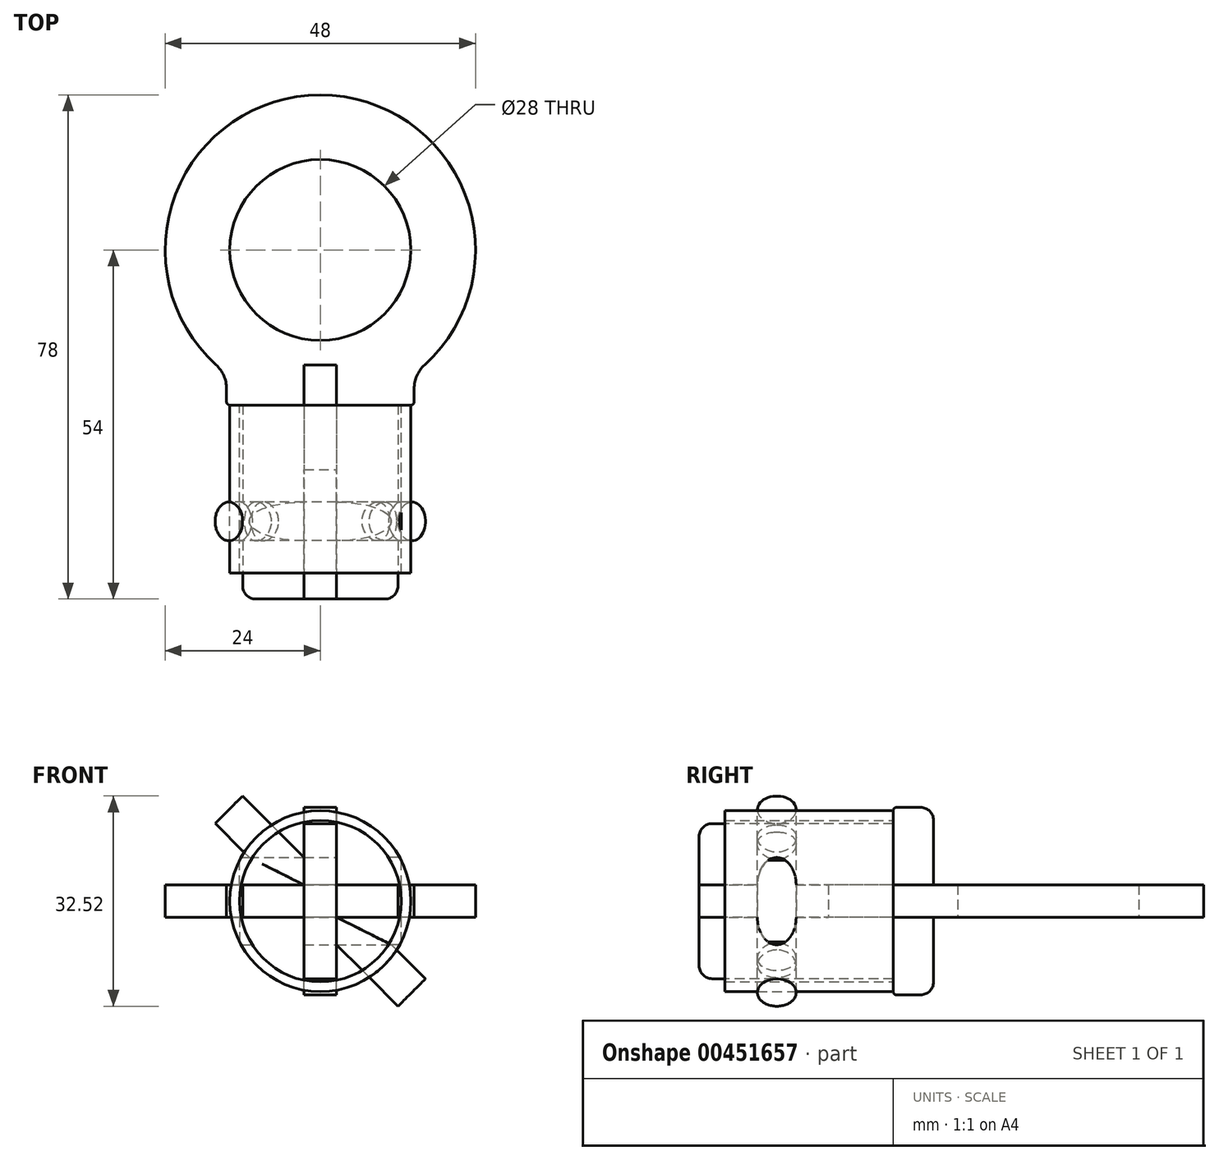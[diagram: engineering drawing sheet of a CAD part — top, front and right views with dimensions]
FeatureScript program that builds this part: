
annotation { "Feature Type Name" : "Feature", "Feature Type Description" : "" }
export const myFeature = defineFeature(function(context is Context, id is Id, definition is map)
    precondition{}
    {
        {
            var Q0;
            Q0=qCreatedBy(makeId("Top.planeOp"),FACE);
            var sketch = newSketch(context, id + "F0", { "sketchPlane" : qUnion([Q0])});
            skArc(sketch, "E0", {"start": v(15.27, -18.51) * mm, "mid": v(0.57, 24) * mm, "end": v(-16.14, -17.76) * mm});
            skLineSegment(sketch, "E1.top", {"start": v(-12, -54) * mm, "end": v(-2.5, -54) * mm});
            skLineSegment(sketch, "E1.left", {"start": v(-12, -24) * mm, "end": v(-12, -54) * mm});
            skCircle(sketch, "E2.converted", {"center": v(0, 0) * mm, "radius": 14 * mm});
            skLineSegment(sketch, "E3.top", {"start": v(-14.5, -24) * mm, "end": v(-12, -24) * mm});
            skLineSegment(sketch, "E3.left", {"start": v(-14.5, -21.47) * mm, "end": v(-14.5, -24) * mm});
            skPoint(sketch, "E4.visualSharp", {"position": v(-14.5, -19.12) * mm});
            skArc(sketch, "E4.filletArc", {"start": v(-14.5, -21.47) * mm, "mid": v(-14.93, -19.44) * mm, "end": v(-16.14, -17.76) * mm});
            skLineSegment(sketch, "E5.left", {"start": v(-2.5, -54) * mm, "end": v(-2.5, -34) * mm});
            skLineSegment(sketch, "E6", {"start": v(0, 37.75) * mm, "end": v(0, -67.17) * mm, "construction": true});
            skLineSegment(sketch, "E7.MirrorCS", {"start": v(14.5, -24) * mm, "end": v(12, -24) * mm});
            skArc(sketch, "E8.MirrorCS", {"start": v(14.5, -21.47) * mm, "mid": v(14.93, -19.44) * mm, "end": v(16.14, -17.76) * mm});
            skLineSegment(sketch, "E9.MirrorCS", {"start": v(14.5, -21.47) * mm, "end": v(14.5, -24) * mm});
            skLineSegment(sketch, "E10.MirrorCS", {"start": v(2.5, -54) * mm, "end": v(2.5, -34) * mm});
            skLineSegment(sketch, "E11.MirrorCS", {"start": v(12, -54) * mm, "end": v(2.5, -54) * mm});
            skPoint(sketch, "E12.MirrorP", {"position": v(14.5, -19.12) * mm});
            skLineSegment(sketch, "E13.MirrorCS", {"start": v(12, -24) * mm, "end": v(12, -54) * mm});
            skLineSegment(sketch, "E14", {"start": v(-2.5, -34) * mm, "end": v(2.5, -34) * mm});
            skSolve(sketch);
        }
        {
            var Q0;
            Q0 = qSketchRegion(id + "F0", true);
            extrude(context, id + "F1", {"entities" : qUnion([Q0]), "endBound" : BoundingType.SYMMETRIC, "depth" : 5 * mm});
        }
        {
            var Q0;
            Q0=qCreatedBy(makeId("Right.planeOp"),FACE);
            var sketch = newSketch(context, id + "F2", { "sketchPlane" : qUnion([Q0])});
            skLineSegment(sketch, "E15.bottom", {"start": v(-24, 12) * mm, "end": v(-54, 12) * mm});
            skLineSegment(sketch, "E15.right", {"start": v(-54, 12) * mm, "end": v(-54, -12) * mm});
            skPoint(sketch, "E15.middle", {"position": v(-41.38, 0) * mm});
            skLineSegment(sketch, "E16.bottom", {"start": v(-24, 14.5) * mm, "end": v(-17.76, 14.5) * mm});
            skLineSegment(sketch, "E16.left", {"start": v(-24, 14.5) * mm, "end": v(-24, 12) * mm});
            skLineSegment(sketch, "E16.right", {"start": v(-17.76, 14.5) * mm, "end": v(-17.76, -14.5) * mm});
            skLineSegment(sketch, "E17", {"start": v(27.36, 0) * mm, "end": v(-59.34, 0) * mm, "construction": true});
            skLineSegment(sketch, "E18.MirrorCS", {"start": v(-24, -14.5) * mm, "end": v(-24, -12) * mm});
            skLineSegment(sketch, "E19.MirrorCS", {"start": v(-24, -12) * mm, "end": v(-54, -12) * mm});
            skLineSegment(sketch, "E20.MirrorCS", {"start": v(-24, -14.5) * mm, "end": v(-17.76, -14.5) * mm});
            skSolve(sketch);
        }
        {
            var Q0;
            Q0 = qSketchRegion(id + "F2", true);
            extrude(context, id + "F3", {"entities" : qUnion([Q0]), "endBound" : BoundingType.SYMMETRIC, "depth" : 5 * mm});
        }
        {
            var Q0;
            Q0=makeQuery(id+"F1.opExtrude","SWEPT_BODY",BODY,{"disambiguationData":[OSD([sQuery(id+"F0.wireOp",EDGE,"E0"),sQuery(id+"F0.wireOp",EDGE,"E1.top"),sQuery(id+"F0.wireOp",EDGE,"E1.left"),sQuery(id+"F0.wireOp",EDGE,"E2.converted"),sQuery(id+"F0.wireOp",EDGE,"E3.top"),sQuery(id+"F0.wireOp",EDGE,"E3.left"),sQuery(id+"F0.wireOp",EDGE,"E4.filletArc"),sQuery(id+"F0.wireOp",EDGE,"E5.left"),sQuery(id+"F0.wireOp",EDGE,"E7.MirrorCS"),sQuery(id+"F0.wireOp",EDGE,"E8.MirrorCS"),sQuery(id+"F0.wireOp",EDGE,"E9.MirrorCS"),sQuery(id+"F0.wireOp",EDGE,"E10.MirrorCS"),sQuery(id+"F0.wireOp",EDGE,"E11.MirrorCS"),sQuery(id+"F0.wireOp",EDGE,"E13.MirrorCS"),sQuery(id+"F0.wireOp",EDGE,"E14")])]});
            var Q1;
            Q1=makeQuery(id+"F3.opExtrude","SWEPT_BODY",BODY,{"disambiguationData":[OSD([sQuery(id+"F2.wireOp",EDGE,"E15.bottom"),sQuery(id+"F2.wireOp",EDGE,"E15.right"),sQuery(id+"F2.wireOp",EDGE,"E16.bottom"),sQuery(id+"F2.wireOp",EDGE,"E16.left"),sQuery(id+"F2.wireOp",EDGE,"E16.right"),sQuery(id+"F2.wireOp",EDGE,"E18.MirrorCS"),sQuery(id+"F2.wireOp",EDGE,"E19.MirrorCS"),sQuery(id+"F2.wireOp",EDGE,"E20.MirrorCS")])]});
            booleanBodies(context, id + "F4", {"operationType" : BooleanOperationType.SUBTRACTION, "tools" : qUnion([Q0]), "targets" : qUnion([Q1]), "keepTools" : true});
        }
        {
            var Q0;
            Q0=qCreatedBy(makeId("Front.planeOp"),FACE);
            var sketch = newSketch(context, id + "F5", { "sketchPlane" : qUnion([Q0])});
            skCircle(sketch, "E21", {"center": v(0, 0) * mm, "radius": 12.5 * mm});
            skCircle(sketch, "E22", {"center": v(0, 0) * mm, "radius": 14 * mm});
            skSolve(sketch);
        }
        {
            var Q0;
            Q0 = qSketchRegion(id + "F5", true);
            extrude(context, id + "F6", {"entities" : qUnion([Q0]), "depth" : 50 * mm, "hasSecondDirection" : true, "secondDirectionOppositeDirection" : false, "secondDirectionDepth" : 24 * mm});
        }
        {
            var Q0;
            Q0=qCreatedBy(makeId("Right.planeOp"),FACE);
            var Q1;
            Q1=qCreatedBy(makeId("Top.planeOp"),FACE);
            cPlane(context, id + "F7", {"entities" : qUnion([Q0, Q1]), "cplaneType" : CPlaneType.MID_PLANE, "offset" : 25 * mm, "width" : 150 * mm, "height" : 150 * mm});
        }
        {
            var Q0;
            Q0=qCreatedBy(id+"F7.planeOp",FACE);
            var sketch = newSketch(context, id + "F8", { "sketchPlane" : qUnion([Q0])});
            skCircle(sketch, "E23", {"center": v(-42, 0) * mm, "radius": 3 * mm});
            skSolve(sketch);
        }
        {
            var Q0;
            Q0 = qSketchRegion(id + "F8", true);
            extrude(context, id + "F9", {"entities" : qUnion([Q0]), "endBound" : BoundingType.SYMMETRIC, "depth" : 40 * mm});
        }
        {
            var Q0;
            Q0=makeQuery(id+"F9.opExtrude","SWEPT_BODY",BODY,{"disambiguationData":[OSD([sQuery(id+"F8.wireOp",EDGE,"E23")])]});
            var Q1;
            Q1=makeQuery(id+"F6.opExtrude","SWEPT_BODY",BODY,{"disambiguationData":[OSD([sQuery(id+"F5.wireOp",EDGE,"E21"),sQuery(id+"F5.wireOp",EDGE,"E22")])]});
            booleanBodies(context, id + "F10", {"operationType" : BooleanOperationType.SUBTRACTION, "tools" : qUnion([Q0]), "targets" : qUnion([Q1]), "keepTools" : true});
        }
        {
            var Q0;
            Q0=makeQuery(id+"F9.opExtrude","SWEPT_BODY",BODY,{"disambiguationData":[OSD([sQuery(id+"F8.wireOp",EDGE,"E23")])]});
            var Q1;
            Q1=makeQuery(id+"F3.opExtrude","SWEPT_BODY",BODY,{"disambiguationData":[OSD([sQuery(id+"F2.wireOp",EDGE,"E15.bottom"),sQuery(id+"F2.wireOp",EDGE,"E15.right"),sQuery(id+"F2.wireOp",EDGE,"E16.bottom"),sQuery(id+"F2.wireOp",EDGE,"E16.left"),sQuery(id+"F2.wireOp",EDGE,"E16.right"),sQuery(id+"F2.wireOp",EDGE,"E18.MirrorCS"),sQuery(id+"F2.wireOp",EDGE,"E19.MirrorCS"),sQuery(id+"F2.wireOp",EDGE,"E20.MirrorCS")])]});
            var Q2;
            Q2=makeQuery(id+"F1.opExtrude","SWEPT_BODY",BODY,{"disambiguationData":[OSD([sQuery(id+"F0.wireOp",EDGE,"E0"),sQuery(id+"F0.wireOp",EDGE,"E1.top"),sQuery(id+"F0.wireOp",EDGE,"E1.left"),sQuery(id+"F0.wireOp",EDGE,"E2.converted"),sQuery(id+"F0.wireOp",EDGE,"E3.top"),sQuery(id+"F0.wireOp",EDGE,"E3.left"),sQuery(id+"F0.wireOp",EDGE,"E4.filletArc"),sQuery(id+"F0.wireOp",EDGE,"E5.left"),sQuery(id+"F0.wireOp",EDGE,"E7.MirrorCS"),sQuery(id+"F0.wireOp",EDGE,"E8.MirrorCS"),sQuery(id+"F0.wireOp",EDGE,"E9.MirrorCS"),sQuery(id+"F0.wireOp",EDGE,"E10.MirrorCS"),sQuery(id+"F0.wireOp",EDGE,"E11.MirrorCS"),sQuery(id+"F0.wireOp",EDGE,"E13.MirrorCS"),sQuery(id+"F0.wireOp",EDGE,"E14")])]});
            booleanBodies(context, id + "F11", {"operationType" : BooleanOperationType.SUBTRACTION, "tools" : qUnion([Q0]), "targets" : qUnion([Q1, Q2]), "keepTools" : true});
        }
        {
            var Q0;
            Q0=qCreatedBy(makeId("Top.planeOp"),FACE);
            var sketch = newSketch(context, id + "F12", { "sketchPlane" : qUnion([Q0])});
            skEllipticalArc(sketch, "E24.0", {});
            skEllipticalArc(sketch, "E25.MirrorCS", {});
            skLineSegment(sketch, "E26", {"start": v(-2.5, -39) * mm, "end": v(2.5, -39) * mm});
            skLineSegment(sketch, "E27", {"start": v(2.5, -45) * mm, "end": v(-2.5, -45) * mm});
            const initialGuessF12  = {"E24.0": [-0.0025, -0.042, -1, 0, 0.004242640687119285, 0.003, 4.71238898038469, 1.5707963267948966], "E25.MirrorCS": [0.0025, -0.042, 1, 0, 0.004242640687119285, 0.003, 4.71238898038469, 1.5707963267948966]};
            skSetInitialGuess(sketch, initialGuessF12);
            skSolve(sketch);
        }
        {
            var Q0;
            Q0 = qSketchRegion(id + "F12", true);
            extrude(context, id + "F13", {"entities" : qUnion([Q0]), "endBound" : BoundingType.SYMMETRIC, "depth" : 25 * mm});
        }
        {
            var Q0;
            Q0=makeQuery(id+"F13.opExtrude","SWEPT_BODY",BODY,{"disambiguationData":[OSD([sQuery(id+"F12.wireOp",EDGE,"E24.0"),sQuery(id+"F12.wireOp",EDGE,"E25.MirrorCS"),sQuery(id+"F12.wireOp",EDGE,"E26"),sQuery(id+"F12.wireOp",EDGE,"E27")])]});
            var Q1;
            Q1=makeQuery(id+"F1.opExtrude","SWEPT_BODY",BODY,{"disambiguationData":[OSD([sQuery(id+"F0.wireOp",EDGE,"E0"),sQuery(id+"F0.wireOp",EDGE,"E1.top"),sQuery(id+"F0.wireOp",EDGE,"E1.left"),sQuery(id+"F0.wireOp",EDGE,"E2.converted"),sQuery(id+"F0.wireOp",EDGE,"E3.top"),sQuery(id+"F0.wireOp",EDGE,"E3.left"),sQuery(id+"F0.wireOp",EDGE,"E4.filletArc"),sQuery(id+"F0.wireOp",EDGE,"E5.left"),sQuery(id+"F0.wireOp",EDGE,"E7.MirrorCS"),sQuery(id+"F0.wireOp",EDGE,"E8.MirrorCS"),sQuery(id+"F0.wireOp",EDGE,"E9.MirrorCS"),sQuery(id+"F0.wireOp",EDGE,"E10.MirrorCS"),sQuery(id+"F0.wireOp",EDGE,"E11.MirrorCS"),sQuery(id+"F0.wireOp",EDGE,"E13.MirrorCS"),sQuery(id+"F0.wireOp",EDGE,"E14")])]});
            booleanBodies(context, id + "F14", {"operationType" : BooleanOperationType.SUBTRACTION, "tools" : qUnion([Q0]), "targets" : qUnion([Q1])});
        }
        {
            var Q0;
            Q0=qCreatedBy(makeId("Right.planeOp"),FACE);
            var sketch = newSketch(context, id + "F15", { "sketchPlane" : qUnion([Q0])});
            skEllipticalArc(sketch, "E28.0", {});
            skEllipticalArc(sketch, "E29.MirrorC", {});
            skLineSegment(sketch, "E30", {"start": v(-45, 2.5) * mm, "end": v(-45, -2.5) * mm});
            skLineSegment(sketch, "E31", {"start": v(-39, 2.5) * mm, "end": v(-39, -2.5) * mm});
            const initialGuessF15  = {"E28.0": [-0.042, -0.0025, 0, 1, 0.004242640687119285, 0.003, 1.5707963267948966, 4.71238898038469], "E29.MirrorC": [-0.042, 0.0025, 0, -1, 0.004242640687119285, 0.003, 1.5707963267948966, 4.71238898038469]};
            skSetInitialGuess(sketch, initialGuessF15);
            skSolve(sketch);
        }
        {
            var Q0;
            Q0 = qSketchRegion(id + "F15", true);
            extrude(context, id + "F16", {"entities" : qUnion([Q0]), "operationType" : NewBodyOperationType.REMOVE, "endBound" : BoundingType.SYMMETRIC, "depth" : 25 * mm});
        }
        {
            var Q0;
            Q0=makeQuery(id+"F3.opExtrude","SWEPT_EDGE",EDGE,{"disambiguationData":[OSD([sQuery(id+"F2.wireOp",EDGE,"E15.bottom"),sQuery(id+"F2.wireOp",EDGE,"E15.right")])]});
            var Q1;
            Q1=makeQuery(id+"F1.opExtrude","SWEPT_EDGE",EDGE,{"disambiguationData":[OSD([sQuery(id+"F0.wireOp",EDGE,"E11.MirrorCS"),sQuery(id+"F0.wireOp",EDGE,"E13.MirrorCS")])]});
            var Q2;
            Q2=makeQuery(id+"F1.opExtrude","SWEPT_EDGE",EDGE,{"disambiguationData":[OSD([sQuery(id+"F0.wireOp",EDGE,"E1.top"),sQuery(id+"F0.wireOp",EDGE,"E1.left")])]});
            var Q3;
            Q3=makeQuery(id+"F3.opExtrude","SWEPT_EDGE",EDGE,{"disambiguationData":[OSD([sQuery(id+"F2.wireOp",EDGE,"E15.right"),sQuery(id+"F2.wireOp",EDGE,"E19.MirrorCS")])]});
            fillet(context, id + "F17", {"entities" : qUnion([Q0, Q1, Q2, Q3]), "radius" : 2 * mm, "tangentPropagation" : true, "allowEdgeOverflow" : false});
        }
        {
            var Q0;
            Q0=makeQuery(id+"F3.opExtrude","SWEPT_EDGE",EDGE,{"disambiguationData":[OSD([sQuery(id+"F2.wireOp",EDGE,"E16.right"),sQuery(id+"F2.wireOp",EDGE,"E20.MirrorCS")])]});
            var Q1;
            Q1=makeQuery(id+"F3.opExtrude","SWEPT_EDGE",EDGE,{"disambiguationData":[OSD([sQuery(id+"F2.wireOp",EDGE,"E16.bottom"),sQuery(id+"F2.wireOp",EDGE,"E16.right")])]});
            fillet(context, id + "F18", {"entities" : qUnion([Q0, Q1]), "radius" : 2 * mm, "tangentPropagation" : true, "allowEdgeOverflow" : false});
        }
        {
            var Q0;
            Q0=makeQuery(id+"F3.opExtrude","SWEPT_EDGE",EDGE,{"disambiguationData":[OSD([sQuery(id+"F2.wireOp",EDGE,"E16.bottom"),sQuery(id+"F2.wireOp",EDGE,"E16.left")])]});
            var Q1;
            Q1=makeQuery(id+"F1.opExtrude","SWEPT_EDGE",EDGE,{"disambiguationData":[OSD([sQuery(id+"F0.wireOp",EDGE,"E7.MirrorCS"),sQuery(id+"F0.wireOp",EDGE,"E9.MirrorCS")])]});
            var Q2;
            Q2=makeQuery(id+"F3.opExtrude","SWEPT_EDGE",EDGE,{"disambiguationData":[OSD([sQuery(id+"F2.wireOp",EDGE,"E18.MirrorCS"),sQuery(id+"F2.wireOp",EDGE,"E20.MirrorCS")])]});
            var Q3;
            Q3=makeQuery(id+"F1.opExtrude","SWEPT_EDGE",EDGE,{"disambiguationData":[OSD([sQuery(id+"F0.wireOp",EDGE,"E3.top"),sQuery(id+"F0.wireOp",EDGE,"E3.left")])]});
            fillet(context, id + "F19", {"entities" : qUnion([Q0, Q1, Q2, Q3]), "radius" : 0.5 * mm, "tangentPropagation" : true, "allowEdgeOverflow" : false});
        }
    });
